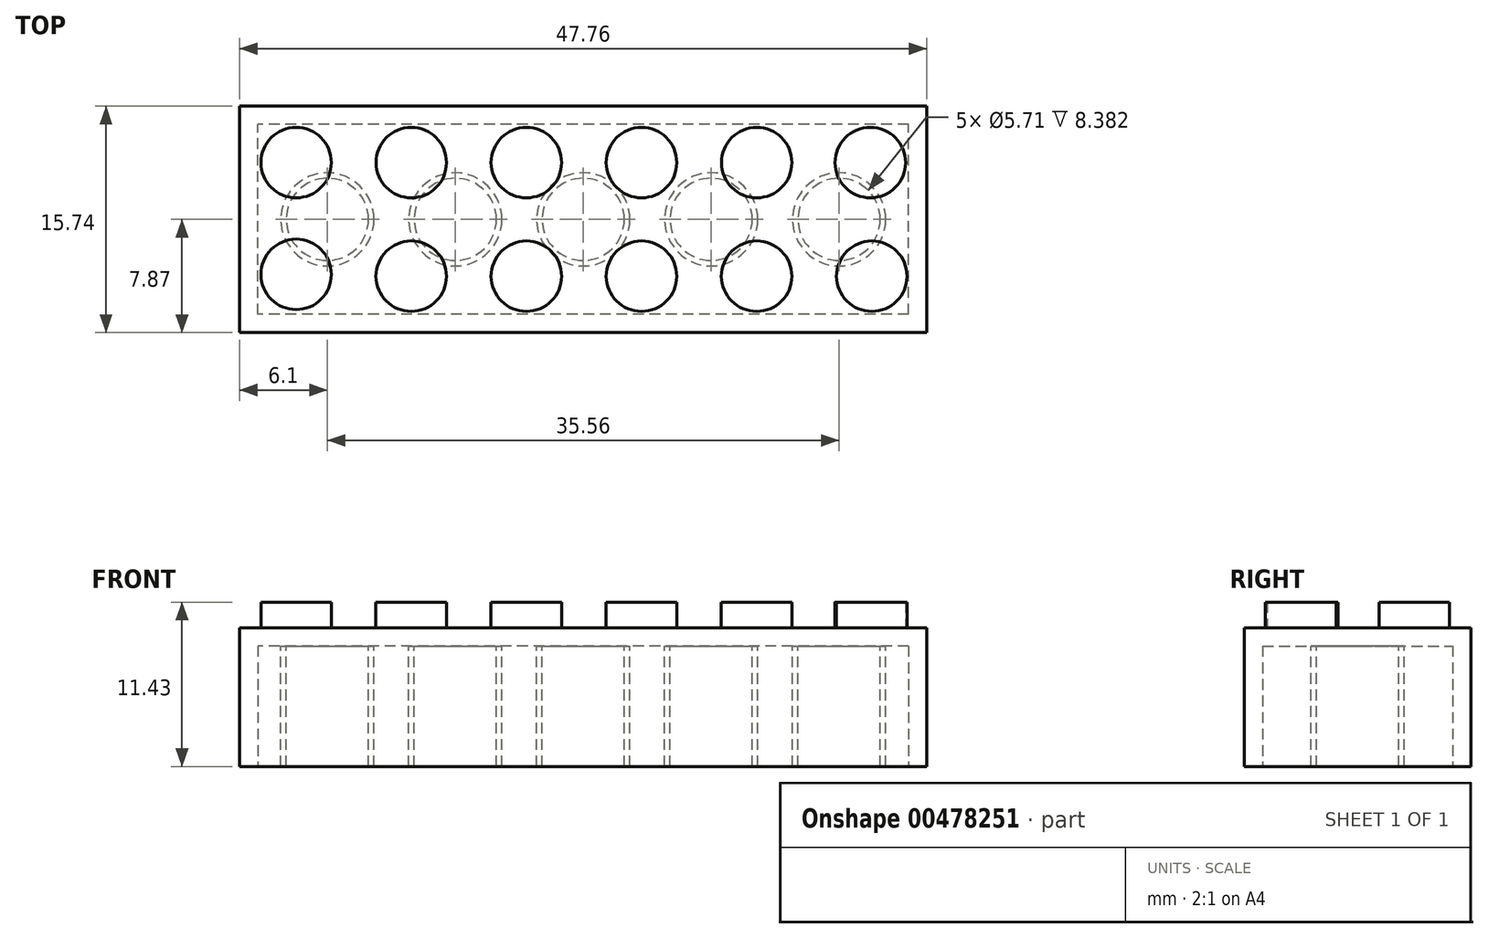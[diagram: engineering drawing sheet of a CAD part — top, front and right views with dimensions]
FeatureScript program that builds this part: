
annotation { "Feature Type Name" : "Feature", "Feature Type Description" : "" }
export const myFeature = defineFeature(function(context is Context, id is Id, definition is map)
    precondition{}
    {
        {
            var Q0;
            Q0=qCreatedBy(makeId("Top.planeOp"),FACE);
            var sketch = newSketch(context, id + "F0", { "sketchPlane" : qUnion([Q0])});
            skLineSegment(sketch, "E0.bottom", {"start": v(23.88, 7.87) * mm, "end": v(-23.88, 7.87) * mm});
            skLineSegment(sketch, "E0.top", {"start": v(23.88, -7.87) * mm, "end": v(-23.88, -7.87) * mm});
            skLineSegment(sketch, "E0.left", {"start": v(23.88, 7.87) * mm, "end": v(23.88, -7.87) * mm});
            skLineSegment(sketch, "E0.right", {"start": v(-23.88, 7.87) * mm, "end": v(-23.88, -7.87) * mm});
            skPoint(sketch, "E0.middle", {"position": v(0, 0) * mm});
            skSolve(sketch);
        }
        {
            var Q0;
            Q0 = qSketchRegion(id + "F0", true);
            extrude(context, id + "F1", {"entities" : qUnion([Q0]), "depth" : 9.65 * mm, "offsetDistance" : 25.4 * mm});
        }
        {
            var Q0;
            Q0=makeQuery(id+"F1.opExtrude","CAP_FACE",FACE,{"disambiguationData":[OSD([sQuery(id+"F0.wireOp",EDGE,"E0.bottom"),sQuery(id+"F0.wireOp",EDGE,"E0.top"),sQuery(id+"F0.wireOp",EDGE,"E0.left"),sQuery(id+"F0.wireOp",EDGE,"E0.right")])],"isStart":false});
            var sketch = newSketch(context, id + "F2", { "sketchPlane" : qUnion([Q0])});
            skCircle(sketch, "E1", {"center": v(-19.95, 3.95) * mm, "radius": 2.45 * mm});
            skCircle(sketch, "E2", {"center": v(-11.95, 3.95) * mm, "radius": 2.45 * mm});
            skCircle(sketch, "E3", {"center": v(-3.95, 3.95) * mm, "radius": 2.45 * mm});
            skCircle(sketch, "E4", {"center": v(4.05, 3.95) * mm, "radius": 2.45 * mm});
            skCircle(sketch, "E5", {"center": v(12.05, 3.95) * mm, "radius": 2.45 * mm});
            skCircle(sketch, "E6", {"center": v(19.95, 3.95) * mm, "radius": 2.45 * mm});
            skCircle(sketch, "E7", {"center": v(-11.95, -3.95) * mm, "radius": 2.45 * mm});
            skCircle(sketch, "E8", {"center": v(-3.95, -3.95) * mm, "radius": 2.45 * mm});
            skCircle(sketch, "E9", {"center": v(4.05, -3.95) * mm, "radius": 2.45 * mm});
            skCircle(sketch, "E10", {"center": v(12.05, -3.95) * mm, "radius": 2.45 * mm});
            skCircle(sketch, "E11", {"center": v(20.05, -3.95) * mm, "radius": 2.45 * mm});
            skCircle(sketch, "E12", {"center": v(-19.95, -3.82) * mm, "radius": 2.45 * mm});
            skSolve(sketch);
        }
        {
            var Q0;
            Q0 = qSketchRegion(id + "F2", true);
            extrude(context, id + "F3", {"entities" : qUnion([Q0]), "operationType" : NewBodyOperationType.ADD, "depth" : 1.78 * mm, "offsetDistance" : 25.4 * mm});
        }
        {
            var Q0;
            Q0=makeQuery(id+"F1.opExtrude","CAP_FACE",FACE,{"disambiguationData":[OSD([sQuery(id+"F0.wireOp",EDGE,"E0.bottom"),sQuery(id+"F0.wireOp",EDGE,"E0.top"),sQuery(id+"F0.wireOp",EDGE,"E0.left"),sQuery(id+"F0.wireOp",EDGE,"E0.right")])],"isStart":true});
            var sketch = newSketch(context, id + "F4", { "sketchPlane" : qUnion([Q0])});
            skLineSegment(sketch, "E13.bottom", {"start": v(22.6, 6.6) * mm, "end": v(-22.6, 6.6) * mm});
            skLineSegment(sketch, "E13.top", {"start": v(22.6, -6.6) * mm, "end": v(-22.6, -6.6) * mm});
            skLineSegment(sketch, "E13.left", {"start": v(22.6, 6.6) * mm, "end": v(22.6, -6.6) * mm});
            skLineSegment(sketch, "E13.right", {"start": v(-22.6, 6.6) * mm, "end": v(-22.6, -6.6) * mm});
            skPoint(sketch, "E13.middle", {"position": v(0, 0) * mm});
            skSolve(sketch);
        }
        {
            var Q0;
            Q0 = qSketchRegion(id + "F4", true);
            extrude(context, id + "F5", {"entities" : qUnion([Q0]), "operationType" : NewBodyOperationType.REMOVE, "oppositeDirection" : true, "depth" : 8.38 * mm, "offsetDistance" : 25.4 * mm});
        }
        {
            var Q0;
            Q0=makeQuery(id+"F5.boolean.opBoolean","COPY",FACE,{"derivedFrom":makeQuery(id+"F5.opExtrude","CAP_FACE",FACE,{"disambiguationData":[OSD([sQuery(id+"F4.wireOp",EDGE,"E13.bottom"),sQuery(id+"F4.wireOp",EDGE,"E13.top"),sQuery(id+"F4.wireOp",EDGE,"E13.left"),sQuery(id+"F4.wireOp",EDGE,"E13.right")])],"isStart":false})});
            var sketch = newSketch(context, id + "F6", { "sketchPlane" : qUnion([Q0])});
            skCircle(sketch, "E14", {"center": v(-17.78, 0) * mm, "radius": 3.24 * mm});
            skCircle(sketch, "E15", {"center": v(-8.9, 0) * mm, "radius": 3.24 * mm});
            skCircle(sketch, "E16", {"center": v(0, 0) * mm, "radius": 3.24 * mm});
            skCircle(sketch, "E17", {"center": v(8.9, 0) * mm, "radius": 3.24 * mm});
            skCircle(sketch, "E18", {"center": v(17.78, 0) * mm, "radius": 3.24 * mm});
            skCircle(sketch, "E19", {"center": v(-17.78, 0) * mm, "radius": 2.86 * mm});
            skCircle(sketch, "E20", {"center": v(-8.9, 0) * mm, "radius": 2.86 * mm});
            skCircle(sketch, "E21", {"center": v(0, 0) * mm, "radius": 2.86 * mm});
            skCircle(sketch, "E22", {"center": v(8.9, 0) * mm, "radius": 2.86 * mm});
            skCircle(sketch, "E23", {"center": v(17.78, 0) * mm, "radius": 2.86 * mm});
            skSolve(sketch);
        }
        {
            var Q0;
            Q0 = qSketchRegion(id + "F6", true);
            extrude(context, id + "F7", {"entities" : qUnion([Q0]), "operationType" : NewBodyOperationType.ADD, "depth" : 8.38 * mm, "offsetDistance" : 25.4 * mm});
        }
    });
